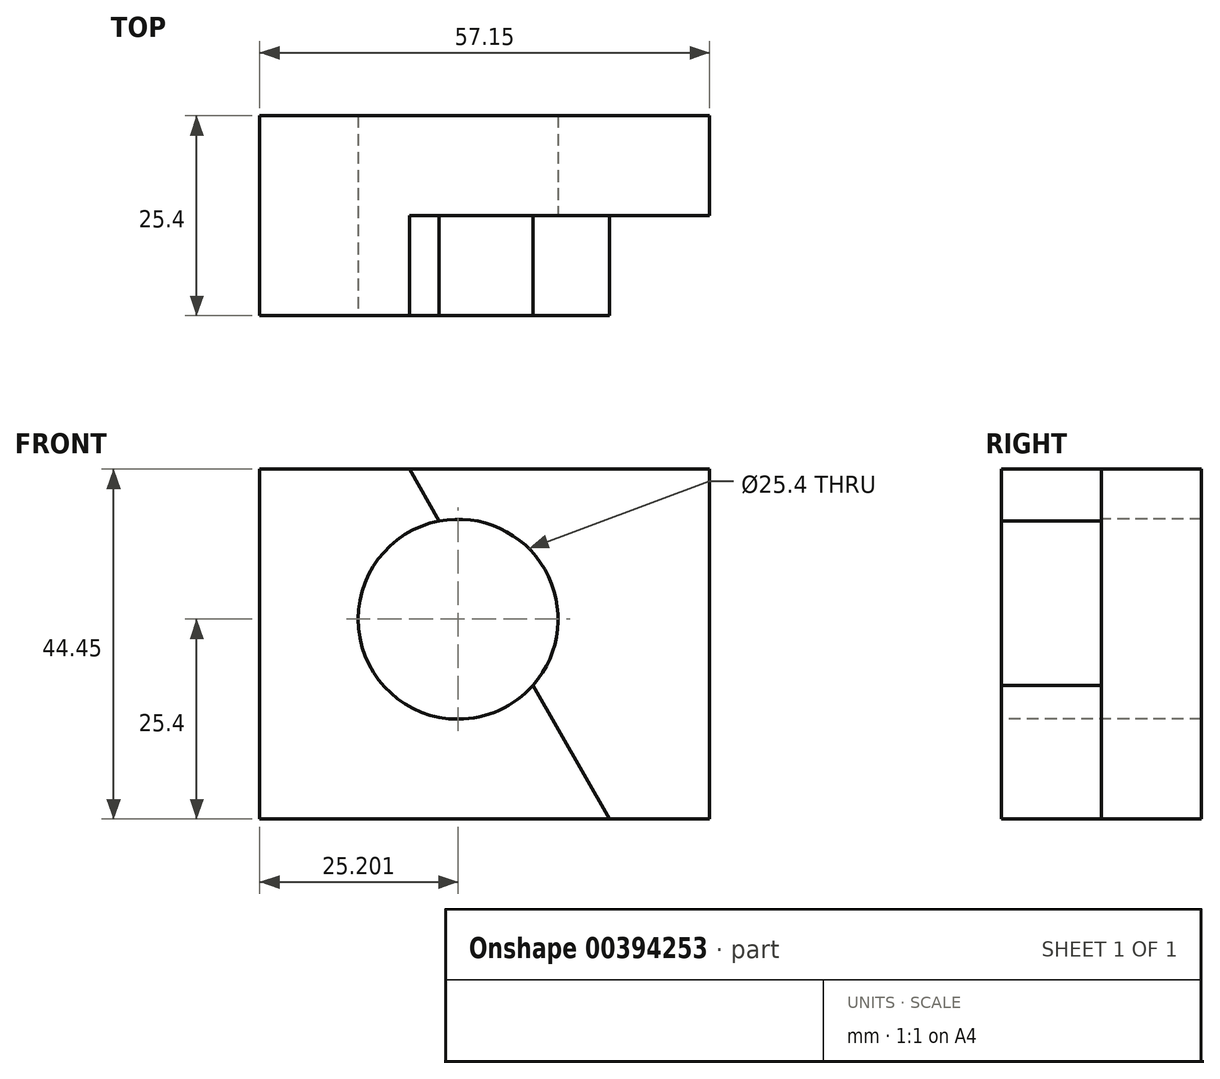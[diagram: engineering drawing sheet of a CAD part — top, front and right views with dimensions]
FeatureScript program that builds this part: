
annotation { "Feature Type Name" : "Feature", "Feature Type Description" : "" }
export const myFeature = defineFeature(function(context is Context, id is Id, definition is map)
    precondition{}
    {
        {
            var Q0;
            Q0=qCreatedBy(makeId("Front.planeOp"),FACE);
            var sketch = newSketch(context, id + "F0", { "sketchPlane" : qUnion([Q0])});
            skLineSegment(sketch, "E0.bottom", {"start": v(0, 0) * mm, "end": v(57.15, 0) * mm});
            skLineSegment(sketch, "E0.top", {"start": v(0, 44.45) * mm, "end": v(57.15, 44.45) * mm});
            skLineSegment(sketch, "E0.left", {"start": v(0, 0) * mm, "end": v(0, 44.45) * mm});
            skLineSegment(sketch, "E0.right", {"start": v(57.15, 0) * mm, "end": v(57.15, 44.45) * mm});
            skSolve(sketch);
        }
        {
            var Q0;
            Q0=makeQuery(id+"F0.imprint","IMPRINT",FACE,{"disambiguationData":[TD([[makeQuery(id+"F0.imprint","IMPRINT",EDGE,{"derivedFrom":sQuery(id+"F0.wireOp",EDGE,"E0.bottom")}),1.0]])]});
            extrude(context, id + "F1", {"entities" : qUnion([Q0]), "depth" : 12.7 * mm});
        }
        {
            var Q0;
            Q0=makeQuery(id+"F1.opExtrude","CAP_FACE",FACE,{"disambiguationData":[OSD([sQuery(id+"F0.wireOp",EDGE,"E0.bottom"),sQuery(id+"F0.wireOp",EDGE,"E0.top"),sQuery(id+"F0.wireOp",EDGE,"E0.left"),sQuery(id+"F0.wireOp",EDGE,"E0.right")])],"isStart":false});
            var sketch = newSketch(context, id + "F2", { "sketchPlane" : qUnion([Q0])});
            skLineSegment(sketch, "E1", {"start": v(0, 44.45) * mm, "end": v(0, 0) * mm});
            skLineSegment(sketch, "E2", {"start": v(0, 0) * mm, "end": v(44.45, 0) * mm});
            skLineSegment(sketch, "E3", {"start": v(44.45, 0) * mm, "end": v(19.05, 44.45) * mm});
            skLineSegment(sketch, "E4", {"start": v(19.05, 44.45) * mm, "end": v(0, 44.45) * mm});
            skSolve(sketch);
        }
        {
            var Q0;
            Q0=makeQuery(id+"F2.imprint","IMPRINT",FACE,{"disambiguationData":[TD([[makeQuery(id+"F2.imprint","IMPRINT",EDGE,{"derivedFrom":sQuery(id+"F2.wireOp",EDGE,"E1")}),-1.0]])]});
            extrude(context, id + "F3", {"entities" : qUnion([Q0]), "operationType" : NewBodyOperationType.ADD, "depth" : 12.7 * mm});
        }
        {
            var Q0;
            Q0=makeQuery(id+"F3.opExtrude","CAP_FACE",FACE,{"disambiguationData":[OSD([sQuery(id+"F2.wireOp",EDGE,"E1"),sQuery(id+"F2.wireOp",EDGE,"E2"),sQuery(id+"F2.wireOp",EDGE,"E3"),sQuery(id+"F2.wireOp",EDGE,"E4")])],"isStart":false});
            var sketch = newSketch(context, id + "F4", { "sketchPlane" : qUnion([Q0])});
            skCircle(sketch, "E5", {"center": v(25.2, 25.4) * mm, "radius": 12.7 * mm});
            skSolve(sketch);
        }
        {
            var Q0;
            {var subQ0=sQuery(id+"F4.wireOp",EDGE,"E5");var subQ1=makeQuery(id+"F3.opExtrude","CAP_EDGE",EDGE,{"disambiguationData":[OSD([sQuery(id+"F2.wireOp",EDGE,"E3")])],"isStart":false});var subQ2=makeQuery(id+"F4.imprint","INTERSECT",VERTEX,{"disambiguationData":[OD(0.0)],"derivedFrom":[subQ1,subQ0]});Q0=makeQuery(id+"F4.imprint","IMPRINT",FACE,{"disambiguationData":[TD([[makeQuery(id+"F4.imprint","IMPRINT",EDGE,{"disambiguationData":[TD([[subQ2,1.0]])],"derivedFrom":subQ0}),1.0]])]});}
            var Q1;
            {var subQ0=sQuery(id+"F4.wireOp",EDGE,"E5");var subQ1=makeQuery(id+"F3.opExtrude","CAP_EDGE",EDGE,{"disambiguationData":[OSD([sQuery(id+"F2.wireOp",EDGE,"E3")])],"isStart":false});var subQ2=makeQuery(id+"F4.imprint","INTERSECT",VERTEX,{"disambiguationData":[OD(0.0)],"derivedFrom":[subQ1,subQ0]});Q1=makeQuery(id+"F4.imprint","IMPRINT",FACE,{"disambiguationData":[TD([[makeQuery(id+"F4.imprint","IMPRINT",EDGE,{"disambiguationData":[TD([[subQ2,-1.0]])],"derivedFrom":subQ0}),1.0]])]});}
            extrude(context, id + "F5", {"entities" : qUnion([Q0, Q1]), "operationType" : NewBodyOperationType.REMOVE, "oppositeDirection" : true, "depth" : 25.4 * mm});
        }
    });
